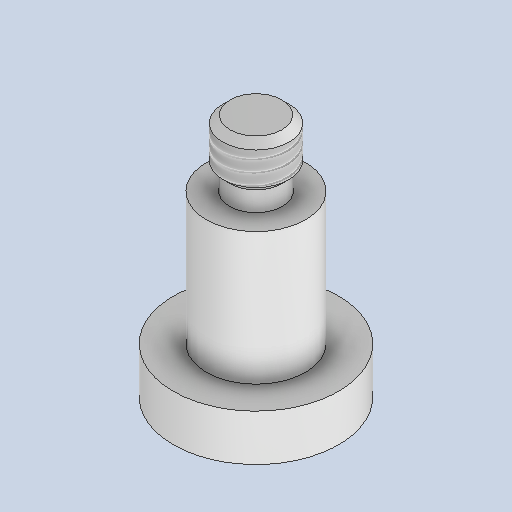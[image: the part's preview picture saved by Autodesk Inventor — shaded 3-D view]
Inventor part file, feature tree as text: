
AUTODESK INVENTOR PART (.ipt)
format: ipt  version: 2024.2 (Build 282272000, 272)  size: 157,696 bytes
history: native  units: mm
features: sketch x2, revolve x1, thread x1, extrude x1, chamfer x1
ambient origin geometry x8: Origin, YZ Plane, XZ Plane, XY Plane, X Axis, Y Axis, Z Axis, Center Point
bodies: Solid1 (feature_tree)
feature tree (6):
  revolve  "Revolution1"  [1 undecoded]
  thread  "Thread1"  [1 undecoded]
  extrude  "Extrusion1"  Depth=2.8mm
  chamfer  "Chamfer1"  Angle=90.0deg  [1 undecoded]
  sketch  "Sketch1"  dims[d0=10.0mm d1=6.0mm d2=4.0mm]
  sketch  "Sketch2"  dims[d4=8.0mm d5=2.8mm d6=90.0deg d7=6.0mm d8=0.0mm d9=2.5mm d10=2.0mm d11=0.0mm d12=0.43mm d13=2.0mm d14=45.0deg d15=4.0mm d16=3.2mm d17=1.2mm d18=45.0deg]
note: 3 required parameter values undecoded (feature->parameter linkage not recoverable at this tier; creation-order binding heuristic only, values carry confidence <= 0.55)